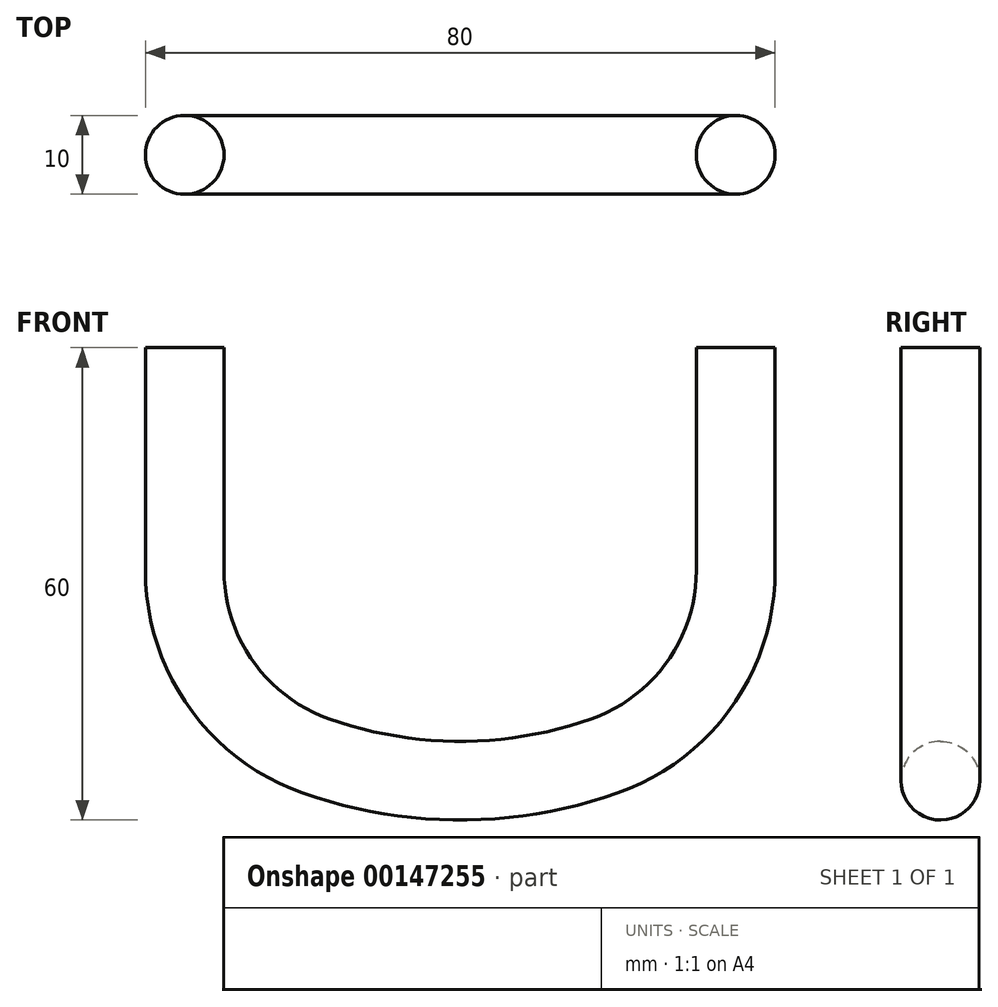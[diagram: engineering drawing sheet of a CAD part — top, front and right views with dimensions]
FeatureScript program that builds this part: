
annotation { "Feature Type Name" : "Feature", "Feature Type Description" : "" }
export const myFeature = defineFeature(function(context is Context, id is Id, definition is map)
    precondition{}
    {
        {
            var Q0;
            Q0=qCreatedBy(makeId("Front.planeOp"),FACE);
            var sketch = newSketch(context, id + "F0", { "sketchPlane" : qUnion([Q0])});
            skLineSegment(sketch, "E0", {"start": v(-35, 22.43) * mm, "end": v(-35, -5.86) * mm});
            skLineSegment(sketch, "E1", {"start": v(35, 22.43) * mm, "end": v(35, -5.86) * mm});
            skPoint(sketch, "E2", {"position": v(0, 22.43) * mm});
            skArc(sketch, "E3", {"start": v(-18.33, -29.43) * mm, "mid": v(0, -32.57) * mm, "end": v(18.33, -29.43) * mm});
            skPoint(sketch, "E4.visualSharp", {"position": v(-35, -20) * mm});
            skArc(sketch, "E4.filletArc", {"start": v(-35, -5.86) * mm, "mid": v(-30.41, -20.29) * mm, "end": v(-18.33, -29.43) * mm});
            skPoint(sketch, "E5.visualSharp", {"position": v(35, -20) * mm});
            skArc(sketch, "E5.filletArc", {"start": v(18.33, -29.43) * mm, "mid": v(30.41, -20.29) * mm, "end": v(35, -5.86) * mm});
            skSolve(sketch);
        }
        {
            var Q0;
            Q0=sQuery(id+"F0.wireOp",VERTEX,"E0.start");
            var Q1;
            Q1=qCreatedBy(makeId("Top.planeOp"),FACE);
            cPlane(context, id + "F1", {"entities" : qUnion([Q0, Q1]), "cplaneType" : CPlaneType.PLANE_POINT, "offset" : 25 * mm, "width" : 150 * mm, "height" : 150 * mm});
        }
        {
            var Q0;
            Q0=qCreatedBy(id+"F1.planeOp",FACE);
            var sketch = newSketch(context, id + "F2", { "sketchPlane" : qUnion([Q0])});
            skPoint(sketch, "E6.0", {"position": v(-35, 0) * mm});
            skCircle(sketch, "E7", {"center": v(-35, 0) * mm, "radius": 5 * mm});
            skSolve(sketch);
        }
        {
            var Q0;
            Q0=makeQuery(id+"F2.imprint","IMPRINT",FACE,{"disambiguationData":[TD([[makeQuery(id+"F2.imprint","IMPRINT",EDGE,{"derivedFrom":sQuery(id+"F2.wireOp",EDGE,"E7")}),1.0]])]});
            var Q1;
            Q1=sQuery(id+"F0.wireOp",EDGE,"E1");
            var Q2;
            Q2=sQuery(id+"F0.wireOp",EDGE,"E5.filletArc");
            var Q3;
            Q3=sQuery(id+"F0.wireOp",EDGE,"E3");
            var Q4;
            Q4=sQuery(id+"F0.wireOp",EDGE,"E4.filletArc");
            var Q5;
            Q5=sQuery(id+"F0.wireOp",EDGE,"E0");
            sweep(context, id + "F3", {"profiles" : qUnion([Q0]), "path" : qUnion([Q1, Q2, Q3, Q4, Q5])});
        }
    });
